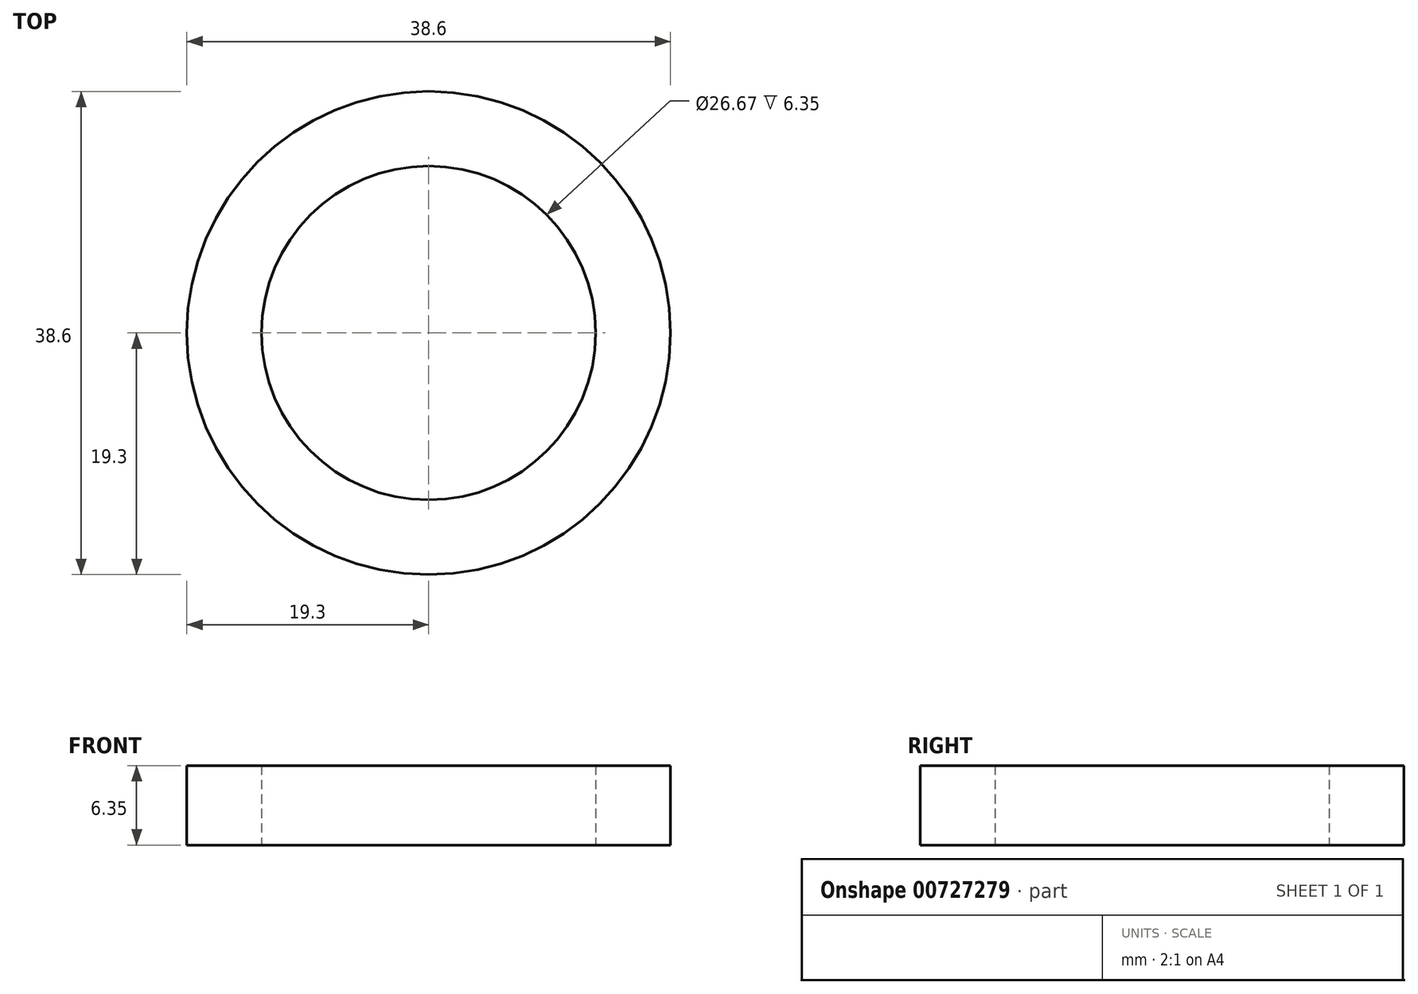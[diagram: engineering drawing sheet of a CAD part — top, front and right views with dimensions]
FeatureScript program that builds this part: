
annotation { "Feature Type Name" : "Feature", "Feature Type Description" : "" }
export const myFeature = defineFeature(function(context is Context, id is Id, definition is map)
    precondition{}
    {
        {
            var Q0;
            Q0=qCreatedBy(makeId("Top.planeOp"),FACE);
            var sketch = newSketch(context, id + "F0", { "sketchPlane" : qUnion([Q0])});
            skCircle(sketch, "E0", {"center": v(0, 0) * mm, "radius": 19.3 * mm});
            skCircle(sketch, "E1", {"center": v(0, 0) * mm, "radius": 13.34 * mm});
            skSolve(sketch);
        }
        {
            var Q0;
            Q0=makeQuery(id+"F0.imprint","IMPRINT",FACE,{"disambiguationData":[TD([[makeQuery(id+"F0.imprint","IMPRINT",EDGE,{"derivedFrom":sQuery(id+"F0.wireOp",EDGE,"E0")}),1.0]])]});
            extrude(context, id + "F1", {"entities" : qUnion([Q0]), "depth" : 6.35 * mm, "offsetDistance" : 25.4 * mm});
        }
    });
